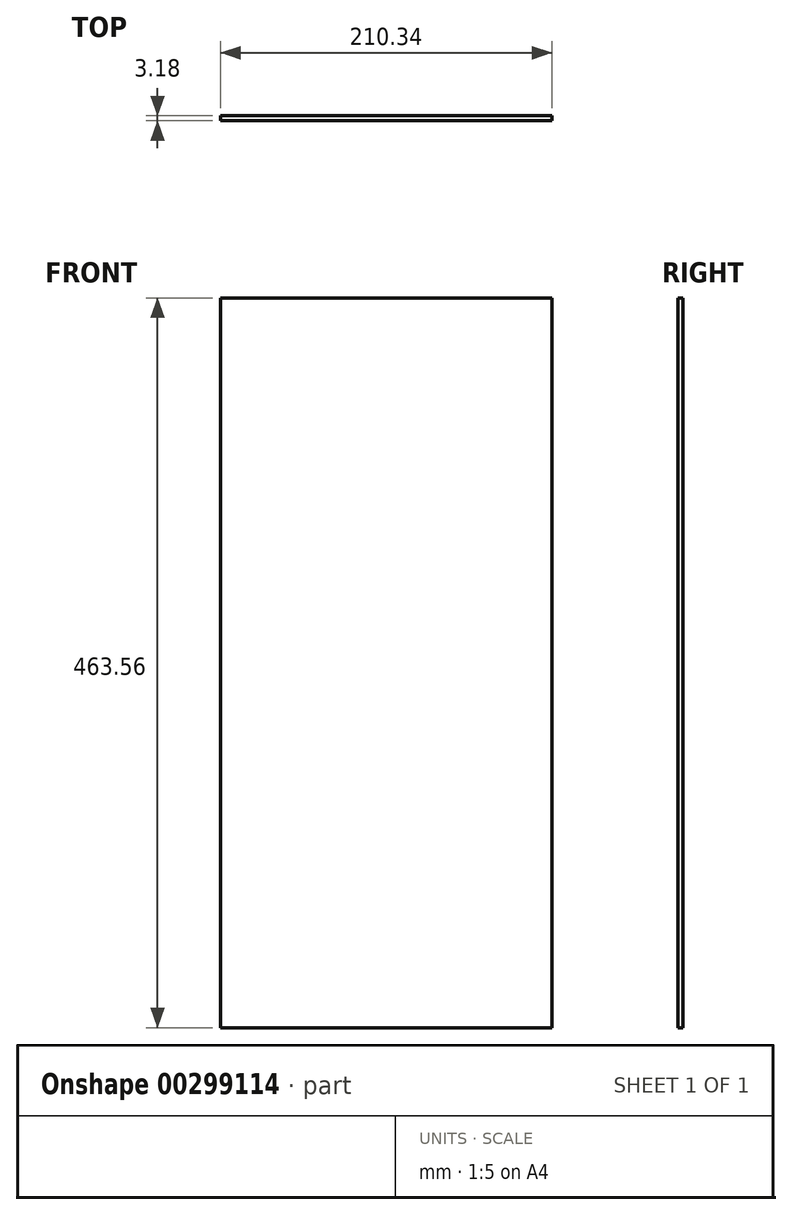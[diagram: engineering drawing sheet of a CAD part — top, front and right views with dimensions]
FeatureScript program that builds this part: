
annotation { "Feature Type Name" : "Feature", "Feature Type Description" : "" }
export const myFeature = defineFeature(function(context is Context, id is Id, definition is map)
    precondition{}
    {
        {
            var Q0;
            Q0=qCreatedBy(makeId("Top.planeOp"),FACE);
            var sketch = newSketch(context, id + "F0", { "sketchPlane" : qUnion([Q0])});
            skLineSegment(sketch, "E0.bottom", {"start": v(105.17, 1.59) * mm, "end": v(-105.17, 1.59) * mm});
            skLineSegment(sketch, "E0.top", {"start": v(105.17, -1.59) * mm, "end": v(-105.17, -1.59) * mm});
            skLineSegment(sketch, "E0.left", {"start": v(105.17, 1.59) * mm, "end": v(105.17, -1.59) * mm});
            skLineSegment(sketch, "E0.right", {"start": v(-105.17, 1.59) * mm, "end": v(-105.17, -1.59) * mm});
            skPoint(sketch, "E0.middle", {"position": v(0, 0) * mm});
            skSolve(sketch);
        }
        {
            var Q0;
            Q0 = qSketchRegion(id + "F0", true);
            extrude(context, id + "F1", {"entities" : qUnion([Q0]), "endBound" : BoundingType.SYMMETRIC, "depth" : 463.55 * mm});
        }
    });
